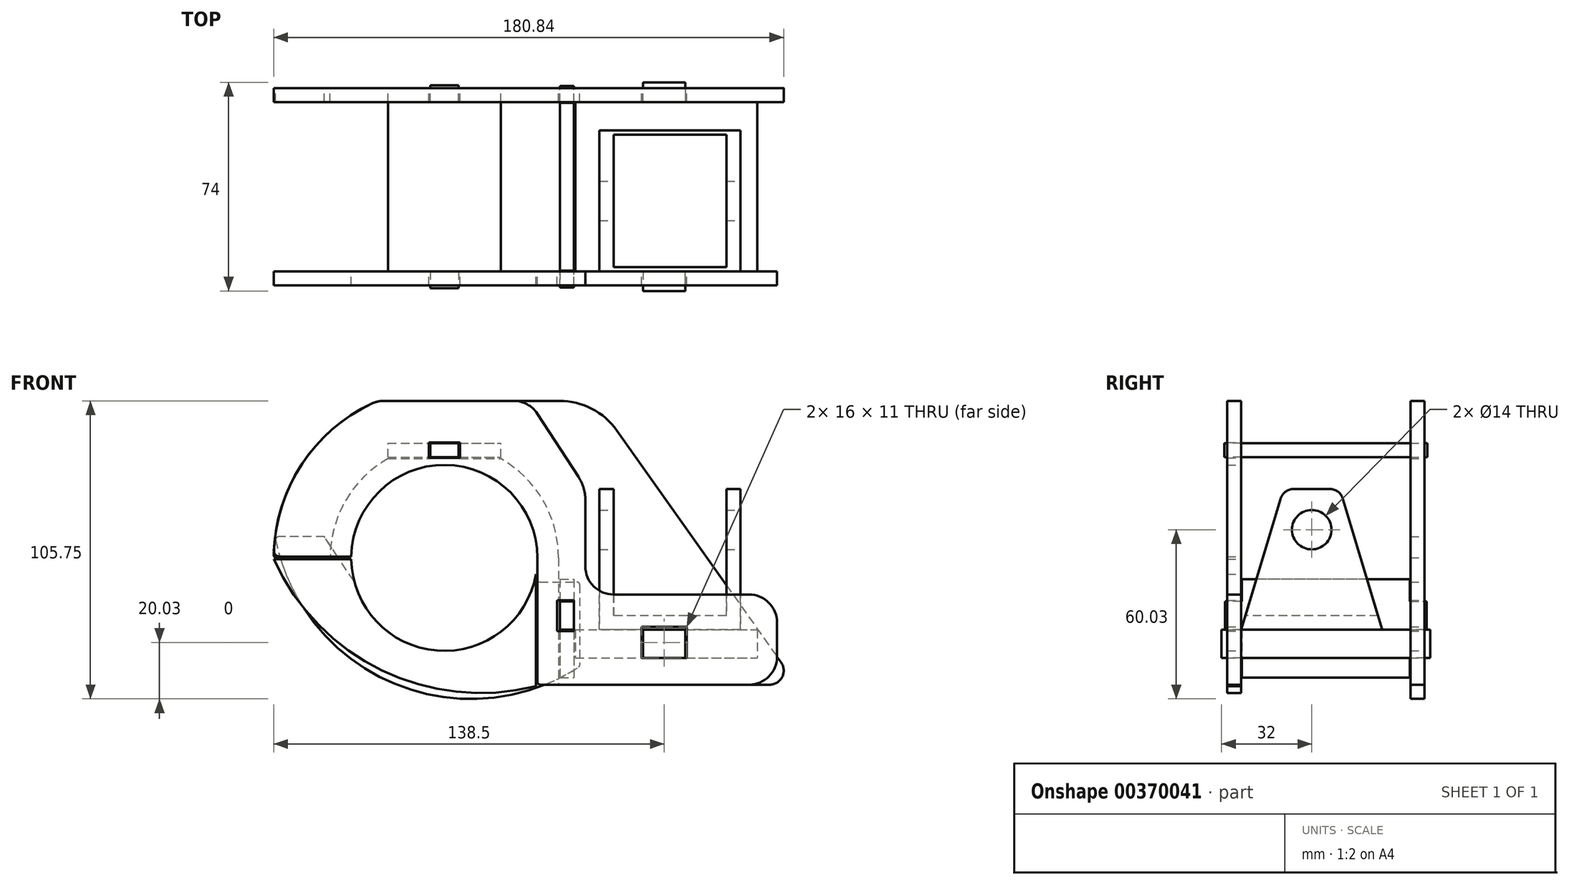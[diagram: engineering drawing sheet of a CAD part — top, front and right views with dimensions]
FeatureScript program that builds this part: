
annotation { "Feature Type Name" : "Feature", "Feature Type Description" : "" }
export const myFeature = defineFeature(function(context is Context, id is Id, definition is map)
    precondition{}
    {
        {
            var Q0;
            Q0=qCreatedBy(makeId("Front.planeOp"),FACE);
            var sketch = newSketch(context, id + "F0", { "sketchPlane" : qUnion([Q0])});
            skArc(sketch, "E0", {"start": v(40.5, 0) * mm, "mid": v(0, 40.5) * mm, "end": v(-40.5, 0) * mm, "construction": true});
            skLineSegment(sketch, "E1", {"start": v(-20, 35.22) * mm, "end": v(-5.5, 35.22) * mm});
            skLineSegment(sketch, "E2", {"start": v(-5.5, 35.22) * mm, "end": v(-5.5, 40.72) * mm});
            skLineSegment(sketch, "E3", {"start": v(-5.5, 40.72) * mm, "end": v(5.5, 40.72) * mm});
            skLineSegment(sketch, "E4", {"start": v(5.5, 40.72) * mm, "end": v(5.5, 35.22) * mm});
            skLineSegment(sketch, "E5", {"start": v(5.5, 35.22) * mm, "end": v(20, 35.22) * mm});
            skPoint(sketch, "E6", {"position": v(0, 40.72) * mm});
            skArc(sketch, "E7", {"start": v(-20, 35.22) * mm, "mid": v(-35, 20.37) * mm, "end": v(-40.5, 0) * mm});
            skArc(sketch, "E8", {"start": v(40.5, 0) * mm, "mid": v(35, 20.37) * mm, "end": v(20, 35.22) * mm});
            skArc(sketch, "E9.0", {"start": v(-25.7, 54.77) * mm, "mid": v(-50.79, 32.87) * mm, "end": v(-60.5, 1.02) * mm});
            skLineSegment(sketch, "E10", {"start": v(-59.5, 0) * mm, "end": v(-40.5, 0) * mm});
            skLineSegment(sketch, "E11", {"start": v(-21.45, 55.72) * mm, "end": v(40.81, 55.72) * mm});
            skLineSegment(sketch, "E12", {"start": v(40.5, 0) * mm, "end": v(40.5, -15) * mm});
            skLineSegment(sketch, "E13", {"start": v(40.5, -45) * mm, "end": v(115.34, -45) * mm});
            skArc(sketch, "E14", {"start": v(-32.5, 0) * mm, "mid": v(0, -32.5) * mm, "end": v(32.5, 0) * mm, "construction": true});
            skLineSegment(sketch, "E15", {"start": v(-40.5, 0) * mm, "end": v(-32.5, 0) * mm, "construction": true});
            skLineSegment(sketch, "E16", {"start": v(40.5, 0) * mm, "end": v(32.5, 0) * mm, "construction": true});
            skPoint(sketch, "E17", {"position": v(80, 10) * mm});
            skLineSegment(sketch, "E18", {"start": v(61.22, 45.15) * mm, "end": v(119.42, -37.11) * mm});
            skLineSegment(sketch, "E19.bottom", {"start": v(70, -24.5) * mm, "end": v(86, -24.5) * mm});
            skLineSegment(sketch, "E19.top", {"start": v(70, -35.5) * mm, "end": v(86, -35.5) * mm});
            skLineSegment(sketch, "E19.left", {"start": v(70, -24.5) * mm, "end": v(70, -35.5) * mm});
            skLineSegment(sketch, "E19.right", {"start": v(86, -24.5) * mm, "end": v(86, -35.5) * mm});
            skPoint(sketch, "E20.visualSharp", {"position": v(-23.58, 55.72) * mm});
            skArc(sketch, "E20.filletArc", {"start": v(-21.45, 55.72) * mm, "mid": v(-23.63, 55.48) * mm, "end": v(-25.7, 54.77) * mm});
            skPoint(sketch, "E21.visualSharp", {"position": v(53.75, 55.72) * mm});
            skArc(sketch, "E21.filletArc", {"start": v(61.22, 45.15) * mm, "mid": v(52.3, 52.92) * mm, "end": v(40.81, 55.72) * mm});
            skPoint(sketch, "E22.visualSharp", {"position": v(125, -45) * mm});
            skArc(sketch, "E22.filletArc", {"start": v(115.34, -45) * mm, "mid": v(119.78, -42.3) * mm, "end": v(119.42, -37.11) * mm});
            skLineSegment(sketch, "E23", {"start": v(40.5, -15) * mm, "end": v(46, -15) * mm});
            skLineSegment(sketch, "E24", {"start": v(46, -15) * mm, "end": v(46, -26) * mm});
            skLineSegment(sketch, "E25", {"start": v(46, -26) * mm, "end": v(40.5, -26) * mm});
            skLineSegment(sketch, "E26.trimOffspring", {"start": v(40.5, -26) * mm, "end": v(40.5, -45) * mm});
            skPoint(sketch, "E27.visualSharp", {"position": v(-60.5, 0) * mm});
            skArc(sketch, "E27.filletArc", {"start": v(-60.5, 1.02) * mm, "mid": v(-60.2, 0.3) * mm, "end": v(-59.5, 0) * mm});
            skSolve(sketch);
        }
        {
            var Q0;
            Q0=qSketchRegion(id+"F0",true);
            var Q1;
            Q1=qConstructionFilter(qBodyType(qCreatedBy(id+"F0",EDGE),BodyType.WIRE),ConstructionObject.NO);
            extrude(context, id + "F1", {"entities" : qUnion([Q0]), "surfaceEntities" : qUnion([Q1]), "depth" : 5 * mm});
        }
        {
            var Q0;
            Q0=qCreatedBy(makeId("Front.planeOp"),FACE);
            var sketch = newSketch(context, id + "F2", { "sketchPlane" : qUnion([Q0])});
            skArc(sketch, "E28", {"start": v(-31.77, -8.91) * mm, "mid": v(-0.7, -33) * mm, "end": v(31.36, -10.26) * mm});
            skLineSegment(sketch, "E29", {"start": v(-31.88, -8.54) * mm, "end": v(0, 0) * mm, "construction": true});
            skLineSegment(sketch, "E30", {"start": v(31.88, -8.54) * mm, "end": v(0, 0) * mm, "construction": true});
            skLineSegment(sketch, "E31", {"start": v(-32.1, -8.2) * mm, "end": v(-42.53, 7.5) * mm});
            skLineSegment(sketch, "E32", {"start": v(-42.53, 7.5) * mm, "end": v(-58.82, 7.5) * mm});
            skLineSegment(sketch, "E33", {"start": v(33.74, -8.54) * mm, "end": v(47, -8.54) * mm});
            skLineSegment(sketch, "E34", {"start": v(48, -9.54) * mm, "end": v(48, -38) * mm});
            skArc(sketch, "E35", {"start": v(-59.8, 6.3) * mm, "mid": v(-18, -44.51) * mm, "end": v(47.54, -38.84) * mm});
            skPoint(sketch, "E36.visualSharp", {"position": v(-31.88, -8.54) * mm});
            skArc(sketch, "E36.filletArc", {"start": v(-31.77, -8.91) * mm, "mid": v(-31.9, -8.55) * mm, "end": v(-32.1, -8.2) * mm});
            skPoint(sketch, "E37.visualSharp", {"position": v(31.88, -8.54) * mm});
            skArc(sketch, "E37.filletArc", {"start": v(33.74, -8.54) * mm, "mid": v(32.27, -9.02) * mm, "end": v(31.36, -10.26) * mm});
            skPoint(sketch, "E38.visualSharp", {"position": v(-60.03, 7.5) * mm});
            skArc(sketch, "E38.filletArc", {"start": v(-58.82, 7.5) * mm, "mid": v(-59.6, 7.13) * mm, "end": v(-59.8, 6.3) * mm});
            skPoint(sketch, "E39.visualSharp", {"position": v(48, -38.54) * mm});
            skArc(sketch, "E39.filletArc", {"start": v(47.54, -38.84) * mm, "mid": v(47.88, -38.48) * mm, "end": v(48, -38) * mm});
            skPoint(sketch, "E40.visualSharp", {"position": v(48, -8.54) * mm});
            skArc(sketch, "E40.filletArc", {"start": v(48, -9.54) * mm, "mid": v(47.7, -8.83) * mm, "end": v(47, -8.54) * mm});
            skSolve(sketch);
        }
        {
            var Q0;
            Q0=qSketchRegion(id+"F2",true);
            extrude(context, id + "F3", {"entities" : qUnion([Q0]), "depth" : 5 * mm});
        }
        {
            var Q0;
            Q0=makeQuery(id+"F1.opExtrude","SWEPT_FACE",FACE,{"disambiguationData":[OSD([sQuery(id+"F0.wireOp",EDGE,"E19.top")])]});
            var sketch = newSketch(context, id + "F4", { "sketchPlane" : qUnion([Q0])});
            skLineSegment(sketch, "E41.bottom", {"start": v(46.5, -5) * mm, "end": v(111, -5) * mm});
            skLineSegment(sketch, "E41.top", {"start": v(46.5, -65) * mm, "end": v(111, -65) * mm});
            skLineSegment(sketch, "E41.left", {"start": v(46.5, -5) * mm, "end": v(46.5, -65) * mm});
            skLineSegment(sketch, "E41.right", {"start": v(111, -5) * mm, "end": v(111, -65) * mm});
            skLineSegment(sketch, "E42", {"start": v(70.5, -5) * mm, "end": v(70.5, 2) * mm});
            skLineSegment(sketch, "E43", {"start": v(70.5, 2) * mm, "end": v(85.5, 2) * mm});
            skLineSegment(sketch, "E44", {"start": v(85.5, 2) * mm, "end": v(85.5, -5) * mm});
            skLineSegment(sketch, "E45", {"start": v(70.5, -65) * mm, "end": v(70.5, -72) * mm});
            skLineSegment(sketch, "E46", {"start": v(70.5, -72) * mm, "end": v(85.5, -72) * mm});
            skLineSegment(sketch, "E47", {"start": v(85.5, -72) * mm, "end": v(85.5, -65) * mm});
            skSolve(sketch);
        }
        {
            var Q0;
            Q0=qSketchRegion(id+"F4",true);
            extrude(context, id + "F5", {"entities" : qUnion([Q0]), "depth" : 10 * mm});
        }
        {
            var Q0;
            {var subQ0=sQuery(id+"F4.wireOp",EDGE,"E41.top");Q0=makeQuery(id+"F5.opExtrude","SWEPT_FACE",FACE,{"disambiguationData":[OSD([subQ0]),TDD([makeQuery(id+"F4.imprint","IMPRINT",EDGE,{"disambiguationData":[TD([[makeQuery(id+"F4.imprint","INTERSECT",VERTEX,{"derivedFrom":[subQ0,sQuery(id+"F4.wireOp",EDGE,"E41.left")]}),-1.0]])],"derivedFrom":subQ0})])]});}
            var sketch = newSketch(context, id + "F6", { "sketchPlane" : qUnion([Q0])});
            skLineSegment(sketch, "E48", {"start": v(60, 24.5) * mm, "end": v(60, -20.5) * mm});
            skLineSegment(sketch, "E49", {"start": v(60, -20.5) * mm, "end": v(100, -20.5) * mm});
            skLineSegment(sketch, "E50", {"start": v(100, -20.5) * mm, "end": v(100, 24.5) * mm});
            skLineSegment(sketch, "E51", {"start": v(100, 24.5) * mm, "end": v(105, 24.5) * mm});
            skLineSegment(sketch, "E52", {"start": v(105, 24.5) * mm, "end": v(105, -25.5) * mm});
            skLineSegment(sketch, "E53", {"start": v(105, -25.5) * mm, "end": v(55, -25.5) * mm});
            skLineSegment(sketch, "E54", {"start": v(55, -25.5) * mm, "end": v(55, 24.5) * mm});
            skLineSegment(sketch, "E55", {"start": v(55, 24.5) * mm, "end": v(60, 24.5) * mm});
            skSolve(sketch);
        }
        {
            var Q0;
            Q0=qSketchRegion(id+"F6",true);
            extrude(context, id + "F7", {"entities" : qUnion([Q0]), "oppositeDirection" : true, "depth" : 50 * mm});
        }
        {
            var Q0;
            Q0=makeQuery(id+"F7.opExtrude","SWEPT_FACE",FACE,{"disambiguationData":[OSD([sQuery(id+"F6.wireOp",EDGE,"E52")])]});
            var sketch = newSketch(context, id + "F8", { "sketchPlane" : qUnion([Q0])});
            skCircle(sketch, "E56", {"center": v(-40, 10) * mm, "radius": 7 * mm});
            skLineSegment(sketch, "E57", {"start": v(-46.28, 24.5) * mm, "end": v(-33.72, 24.5) * mm});
            skPoint(sketch, "E58", {"position": v(-40, 24.5) * mm});
            skLineSegment(sketch, "E59", {"start": v(-65, -25.5) * mm, "end": v(-51.07, 20.94) * mm});
            skLineSegment(sketch, "E60", {"start": v(-28.93, 20.94) * mm, "end": v(-15, -25.5) * mm});
            skPoint(sketch, "E61.visualSharp", {"position": v(-50, 24.5) * mm});
            skArc(sketch, "E61.filletArc", {"start": v(-46.28, 24.5) * mm, "mid": v(-49.26, 23.51) * mm, "end": v(-51.07, 20.94) * mm});
            skPoint(sketch, "E62.visualSharp", {"position": v(-30, 24.5) * mm});
            skArc(sketch, "E62.filletArc", {"start": v(-28.93, 20.94) * mm, "mid": v(-30.74, 23.51) * mm, "end": v(-33.72, 24.5) * mm});
            skLineSegment(sketch, "E63", {"start": v(-46.28, 24.5) * mm, "end": v(-65, 24.5) * mm});
            skLineSegment(sketch, "E64", {"start": v(-65, 24.5) * mm, "end": v(-65, -25.5) * mm});
            skLineSegment(sketch, "E65", {"start": v(-33.72, 24.5) * mm, "end": v(-15, 24.5) * mm});
            skLineSegment(sketch, "E66", {"start": v(-15, 24.5) * mm, "end": v(-15, -25.5) * mm});
            skSolve(sketch);
        }
        {
            var Q0;
            Q0=qSketchRegion(id+"F8",true);
            extrude(context, id + "F9", {"entities" : qUnion([Q0]), "operationType" : NewBodyOperationType.REMOVE, "oppositeDirection" : true, "depth" : 602 * mm});
        }
        {
            var Q0;
            {var subQ0=sQuery(id+"F4.wireOp",EDGE,"E41.top");Q0=makeQuery(id+"F5.opExtrude","SWEPT_FACE",FACE,{"disambiguationData":[OSD([subQ0]),TDD([makeQuery(id+"F4.imprint","IMPRINT",EDGE,{"disambiguationData":[TD([[makeQuery(id+"F4.imprint","INTERSECT",VERTEX,{"derivedFrom":[subQ0,sQuery(id+"F4.wireOp",EDGE,"E41.right")]}),1.0]])],"derivedFrom":subQ0})])]});}
            var sketch = newSketch(context, id + "F10", { "sketchPlane" : qUnion([Q0])});
            skArc(sketch, "E67", {"start": v(33, 0) * mm, "mid": v(0.25, 33) * mm, "end": v(-33, 0.5) * mm});
            skLineSegment(sketch, "E68", {"start": v(-33, 0.5) * mm, "end": v(-58.44, 0.5) * mm});
            skArc(sketch, "E69", {"start": v(-25.7, 54.77) * mm, "mid": v(-50.36, 33.53) * mm, "end": v(-60.44, 2.59) * mm});
            skLineSegment(sketch, "E70", {"start": v(-21.45, 55.72) * mm, "end": v(24.58, 55.72) * mm});
            skPoint(sketch, "E71.orphan", {"position": v(0, 60.5) * mm});
            skLineSegment(sketch, "E72", {"start": v(50, 20.55) * mm, "end": v(50, 0.02) * mm});
            skLineSegment(sketch, "E73", {"start": v(33, 0) * mm, "end": v(33, -44) * mm});
            skLineSegment(sketch, "E74", {"start": v(34, -45) * mm, "end": v(108, -45) * mm});
            skLineSegment(sketch, "E75", {"start": v(118, -35) * mm, "end": v(118, -23) * mm});
            skLineSegment(sketch, "E76", {"start": v(108, -13) * mm, "end": v(60, -13) * mm});
            skLineSegment(sketch, "E77", {"start": v(50, -3) * mm, "end": v(50, 0.02) * mm});
            skLineSegment(sketch, "E78.bottom", {"start": v(70, -24.5) * mm, "end": v(86, -24.5) * mm});
            skLineSegment(sketch, "E78.top", {"start": v(70, -35.5) * mm, "end": v(86, -35.5) * mm});
            skLineSegment(sketch, "E78.left", {"start": v(70, -24.5) * mm, "end": v(70, -35.5) * mm});
            skLineSegment(sketch, "E78.right", {"start": v(86, -24.5) * mm, "end": v(86, -35.5) * mm});
            skPoint(sketch, "E79.visualSharp", {"position": v(-23.57, 55.72) * mm});
            skArc(sketch, "E79.filletArc", {"start": v(-21.45, 55.72) * mm, "mid": v(-23.62, 55.48) * mm, "end": v(-25.7, 54.77) * mm});
            skPoint(sketch, "E80.visualSharp", {"position": v(-60.5, 0.5) * mm});
            skArc(sketch, "E80.filletArc", {"start": v(-60.44, 2.59) * mm, "mid": v(-59.89, 1.12) * mm, "end": v(-58.44, 0.5) * mm});
            skPoint(sketch, "E81.visualSharp", {"position": v(50, 55.72) * mm});
            skPoint(sketch, "E82.visualSharp", {"position": v(50, -13) * mm});
            skArc(sketch, "E82.filletArc", {"start": v(50, -3) * mm, "mid": v(52.93, -10.07) * mm, "end": v(60, -13) * mm});
            skPoint(sketch, "E83.visualSharp", {"position": v(33, -45) * mm});
            skArc(sketch, "E83.filletArc", {"start": v(33, -44) * mm, "mid": v(33.3, -44.7) * mm, "end": v(34, -45) * mm});
            skPoint(sketch, "E84.visualSharp", {"position": v(118, -45) * mm});
            skArc(sketch, "E84.filletArc", {"start": v(108, -45) * mm, "mid": v(115.07, -42.07) * mm, "end": v(118, -35) * mm});
            skPoint(sketch, "E85.visualSharp", {"position": v(118, -13) * mm});
            skArc(sketch, "E85.filletArc", {"start": v(118, -23) * mm, "mid": v(115.07, -15.93) * mm, "end": v(108, -13) * mm});
            skLineSegment(sketch, "E86", {"start": v(32.96, 51.17) * mm, "end": v(47.57, 28.73) * mm});
            skPoint(sketch, "E87.visualSharp", {"position": v(50, 25) * mm});
            skArc(sketch, "E87.filletArc", {"start": v(50, 20.55) * mm, "mid": v(49.38, 24.82) * mm, "end": v(47.57, 28.73) * mm});
            skPoint(sketch, "E88.visualSharp", {"position": v(30, 55.72) * mm});
            skArc(sketch, "E88.filletArc", {"start": v(32.96, 51.17) * mm, "mid": v(29.34, 54.5) * mm, "end": v(24.58, 55.72) * mm});
            skArc(sketch, "E89", {"start": v(-33, -0.5) * mm, "mid": v(-2.62, -32.9) * mm, "end": v(32.5, -5.72) * mm});
            skLineSegment(sketch, "E90", {"start": v(32.5, -5.72) * mm, "end": v(32.5, -45.5) * mm});
            skLineSegment(sketch, "E91", {"start": v(-60.5, -0.5) * mm, "end": v(-33, -0.5) * mm});
            skArc(sketch, "E92", {"start": v(-60.5, -0.5) * mm, "mid": v(-22.18, -39.92) * mm, "end": v(32.5, -45.5) * mm});
            skLineSegment(sketch, "E93.bottom", {"start": v(-5.5, 35.5) * mm, "end": v(5.5, 35.5) * mm});
            skLineSegment(sketch, "E93.top", {"start": v(-5.5, 41) * mm, "end": v(5.5, 41) * mm});
            skLineSegment(sketch, "E93.left", {"start": v(-5.5, 35.5) * mm, "end": v(-5.5, 41) * mm});
            skLineSegment(sketch, "E93.right", {"start": v(5.5, 35.5) * mm, "end": v(5.5, 41) * mm});
            skPoint(sketch, "E94", {"position": v(0, 35.5) * mm});
            skLineSegment(sketch, "E95.bottom", {"start": v(40, -15) * mm, "end": v(46, -15) * mm});
            skLineSegment(sketch, "E95.top", {"start": v(40, -26) * mm, "end": v(46, -26) * mm});
            skLineSegment(sketch, "E95.left", {"start": v(40, -15) * mm, "end": v(40, -26) * mm});
            skLineSegment(sketch, "E95.right", {"start": v(46, -15) * mm, "end": v(46, -26) * mm});
            skSolve(sketch);
        }
        {
            var Q0;
            Q0=qSketchRegion(id+"F10",true);
            extrude(context, id + "F11", {"entities" : qUnion([Q0]), "depth" : 5 * mm});
        }
        {
            var Q0;
            Q0=makeQuery(id+"F1.opExtrude","SWEPT_FACE",FACE,{"disambiguationData":[OSD([sQuery(id+"F0.wireOp",EDGE,"E3")])]});
            var sketch = newSketch(context, id + "F12", { "sketchPlane" : qUnion([Q0])});
            skLineSegment(sketch, "E96.bottom", {"start": v(-20, 5) * mm, "end": v(20, 5) * mm});
            skLineSegment(sketch, "E96.top", {"start": v(-20, 65) * mm, "end": v(20, 65) * mm});
            skLineSegment(sketch, "E96.left", {"start": v(-20, 5) * mm, "end": v(-20, 65) * mm});
            skLineSegment(sketch, "E96.right", {"start": v(20, 5) * mm, "end": v(20, 65) * mm});
            skLineSegment(sketch, "E97.bottom", {"start": v(-5, 5) * mm, "end": v(5, 5) * mm});
            skLineSegment(sketch, "E97.top", {"start": v(-5, -1) * mm, "end": v(5, -1) * mm});
            skLineSegment(sketch, "E97.left", {"start": v(-5, 5) * mm, "end": v(-5, -1) * mm});
            skLineSegment(sketch, "E97.right", {"start": v(5, 5) * mm, "end": v(5, -1) * mm});
            skLineSegment(sketch, "E98.bottom", {"start": v(-5, 65) * mm, "end": v(5, 65) * mm});
            skLineSegment(sketch, "E98.top", {"start": v(-5, 71) * mm, "end": v(5, 71) * mm});
            skLineSegment(sketch, "E98.left", {"start": v(-5, 65) * mm, "end": v(-5, 71) * mm});
            skLineSegment(sketch, "E98.right", {"start": v(5, 65) * mm, "end": v(5, 71) * mm});
            skSolve(sketch);
        }
        {
            var Q0;
            Q0=qSketchRegion(id+"F12",true);
            extrude(context, id + "F13", {"entities" : qUnion([Q0]), "depth" : 5 * mm});
        }
        {
            var Q0;
            Q0=makeQuery(id+"F1.opExtrude","SWEPT_FACE",FACE,{"disambiguationData":[OSD([sQuery(id+"F0.wireOp",EDGE,"E24")])]});
            var sketch = newSketch(context, id + "F14", { "sketchPlane" : qUnion([Q0])});
            skLineSegment(sketch, "E99.bottom", {"start": v(5.25, -7.5) * mm, "end": v(64.75, -7.5) * mm});
            skLineSegment(sketch, "E99.top", {"start": v(5.25, -42.5) * mm, "end": v(64.75, -42.5) * mm});
            skLineSegment(sketch, "E99.left", {"start": v(5.25, -7.5) * mm, "end": v(5.25, -42.5) * mm});
            skLineSegment(sketch, "E99.right", {"start": v(64.75, -7.5) * mm, "end": v(64.75, -42.5) * mm});
            skLineSegment(sketch, "E100.bottom", {"start": v(5.25, -15.5) * mm, "end": v(-0.75, -15.5) * mm});
            skLineSegment(sketch, "E100.top", {"start": v(5.25, -25.5) * mm, "end": v(-0.75, -25.5) * mm});
            skLineSegment(sketch, "E100.left", {"start": v(5.25, -15.5) * mm, "end": v(5.25, -25.5) * mm});
            skLineSegment(sketch, "E100.right", {"start": v(-0.75, -15.5) * mm, "end": v(-0.75, -25.5) * mm});
            skLineSegment(sketch, "E101.bottom", {"start": v(64.75, -15.5) * mm, "end": v(70.75, -15.5) * mm});
            skLineSegment(sketch, "E101.left", {"start": v(64.75, -15.5) * mm, "end": v(64.75, -26) * mm});
            skLineSegment(sketch, "E101.right", {"start": v(70.75, -15.5) * mm, "end": v(70.75, -25.5) * mm});
            skLineSegment(sketch, "E102", {"start": v(70.75, -25.5) * mm, "end": v(64.75, -25.5) * mm});
            skSolve(sketch);
        }
        {
            var Q0;
            Q0=qSketchRegion(id+"F14",true);
            extrude(context, id + "F15", {"entities" : qUnion([Q0]), "depth" : 5 * mm});
        }
    });
